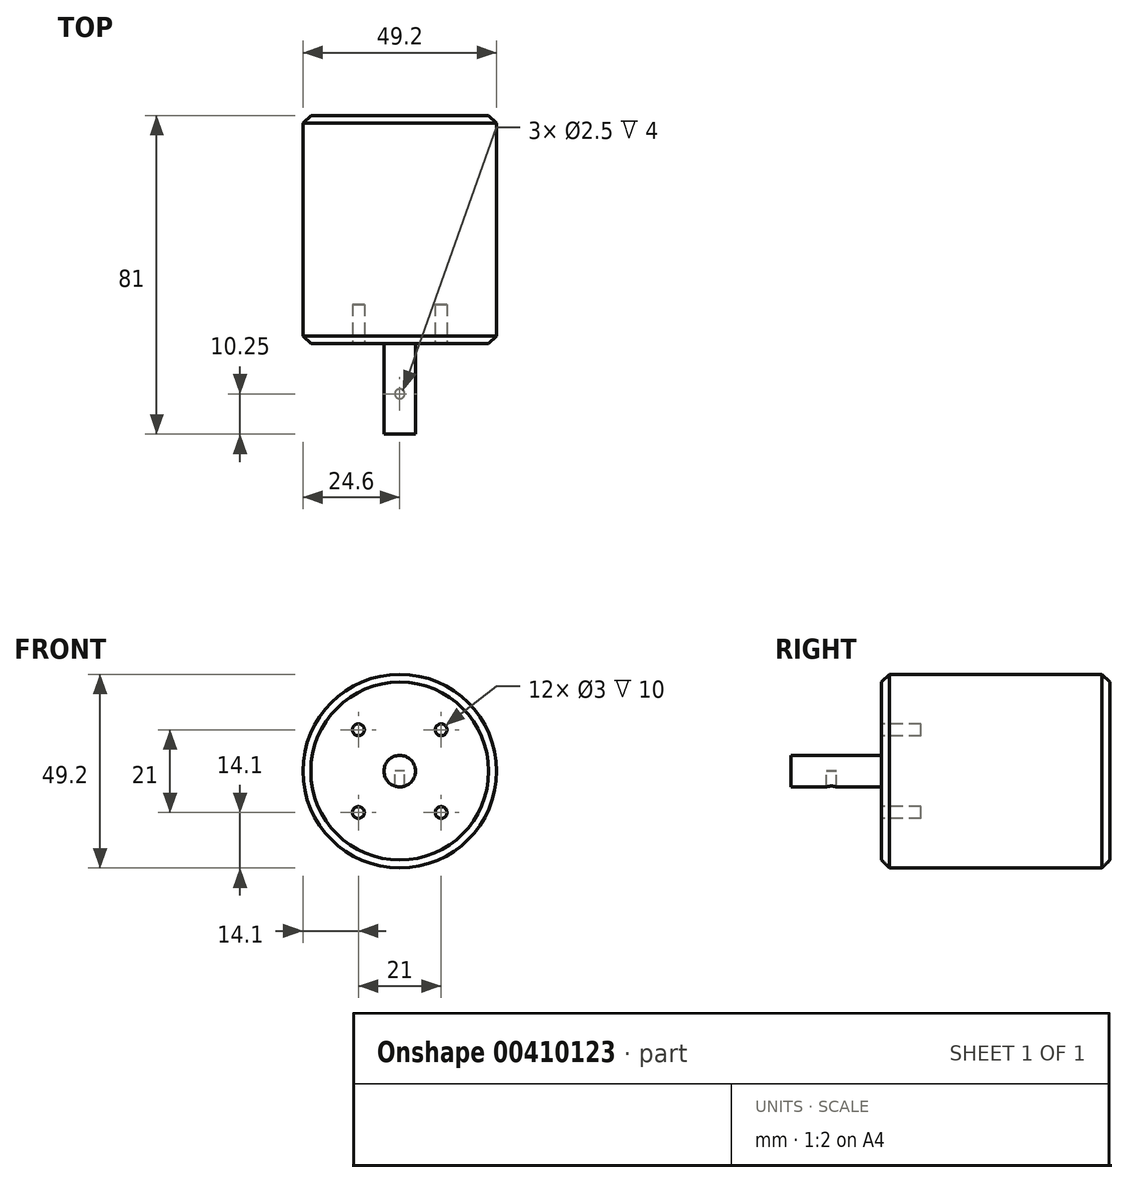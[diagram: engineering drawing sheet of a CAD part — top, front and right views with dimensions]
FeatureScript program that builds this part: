
annotation { "Feature Type Name" : "Feature", "Feature Type Description" : "" }
export const myFeature = defineFeature(function(context is Context, id is Id, definition is map)
    precondition{}
    {
        {
            var Q0;
            Q0=qCreatedBy(makeId("Front.planeOp"),FACE);
            var sketch = newSketch(context, id + "F0", { "sketchPlane" : qUnion([Q0])});
            skCircle(sketch, "E0", {"center": v(0, 0) * mm, "radius": 24.6 * mm});
            skSolve(sketch);
        }
        {
            var Q0;
            Q0=makeQuery(id+"F0.imprint","IMPRINT",FACE,{"disambiguationData":[TD([[makeQuery(id+"F0.imprint","IMPRINT",EDGE,{"derivedFrom":sQuery(id+"F0.wireOp",EDGE,"E0")}),1.0]])]});
            extrude(context, id + "F1", {"entities" : qUnion([Q0]), "depth" : 58 * mm});
        }
        {
            var Q0;
            Q0=makeQuery(id+"F1.opExtrude","CAP_FACE",FACE,{"disambiguationData":[OSD([sQuery(id+"F0.wireOp",EDGE,"E0")])],"isStart":false});
            var sketch = newSketch(context, id + "F2", { "sketchPlane" : qUnion([Q0])});
            skCircle(sketch, "E1", {"center": v(0, 0) * mm, "radius": 4 * mm});
            skSolve(sketch);
        }
        {
            var Q0;
            Q0=qSketchRegion(id+"F2",true);
            var Q1;
            Q1=sQuery(id+"F2.wireOp",EDGE,"E1");
            extrude(context, id + "F3", {"entities" : qUnion([Q0]), "surfaceEntities" : qUnion([Q1]), "depth" : 23 * mm});
        }
        {
            var Q0;
            Q0=makeQuery(id+"F1.opExtrude","CAP_FACE",FACE,{"disambiguationData":[OSD([sQuery(id+"F0.wireOp",EDGE,"E0")])],"isStart":false});
            var sketch = newSketch(context, id + "F4", { "sketchPlane" : qUnion([Q0])});
            skLineSegment(sketch, "E2.bottom", {"start": v(10.5, -10.5) * mm, "end": v(-10.5, -10.5) * mm, "construction": true});
            skLineSegment(sketch, "E2.top", {"start": v(10.5, 10.5) * mm, "end": v(-10.5, 10.5) * mm, "construction": true});
            skLineSegment(sketch, "E2.left", {"start": v(10.5, -10.5) * mm, "end": v(10.5, 10.5) * mm, "construction": true});
            skLineSegment(sketch, "E2.right", {"start": v(-10.5, -10.5) * mm, "end": v(-10.5, 10.5) * mm, "construction": true});
            skPoint(sketch, "E2.middle", {"position": v(0, 0) * mm});
            skCircle(sketch, "E3", {"center": v(10.5, 10.5) * mm, "radius": 1.5 * mm});
            skCircle(sketch, "E4", {"center": v(10.5, -10.5) * mm, "radius": 1.5 * mm});
            skCircle(sketch, "E5", {"center": v(-10.5, -10.5) * mm, "radius": 1.5 * mm});
            skCircle(sketch, "E6", {"center": v(-10.5, 10.5) * mm, "radius": 1.5 * mm});
            skSolve(sketch);
        }
        {
            var Q0;
            Q0=qSketchRegion(id+"F4",true);
            extrude(context, id + "F5", {"entities" : qUnion([Q0]), "operationType" : NewBodyOperationType.REMOVE, "oppositeDirection" : true, "depth" : 10 * mm});
        }
        {
            var Q0;
            Q0=makeQuery(id+"F1.opExtrude","CAP_EDGE",EDGE,{"disambiguationData":[OSD([sQuery(id+"F0.wireOp",EDGE,"E0")])],"isStart":true});
            var Q1;
            Q1=makeQuery(id+"F1.opExtrude","CAP_EDGE",EDGE,{"disambiguationData":[OSD([sQuery(id+"F0.wireOp",EDGE,"E0")])],"isStart":false});
            chamfer(context, id + "F6", {"entities" : qUnion([Q0, Q1]), "width" : 2 * mm, "tangentPropagation" : true});
        }
        {
            var Q0;
            Q0=qCreatedBy(makeId("Top.planeOp"),FACE);
            var sketch = newSketch(context, id + "F7", { "sketchPlane" : qUnion([Q0])});
            skCircle(sketch, "E7", {"center": v(0, -70.75) * mm, "radius": 1.25 * mm});
            skSolve(sketch);
        }
        {
            var Q0;
            Q0 = qSketchRegion(id + "F7", true);
            extrude(context, id + "F8", {"entities" : qUnion([Q0]), "operationType" : NewBodyOperationType.REMOVE, "oppositeDirection" : true, "depth" : 4 * mm});
        }
    });
